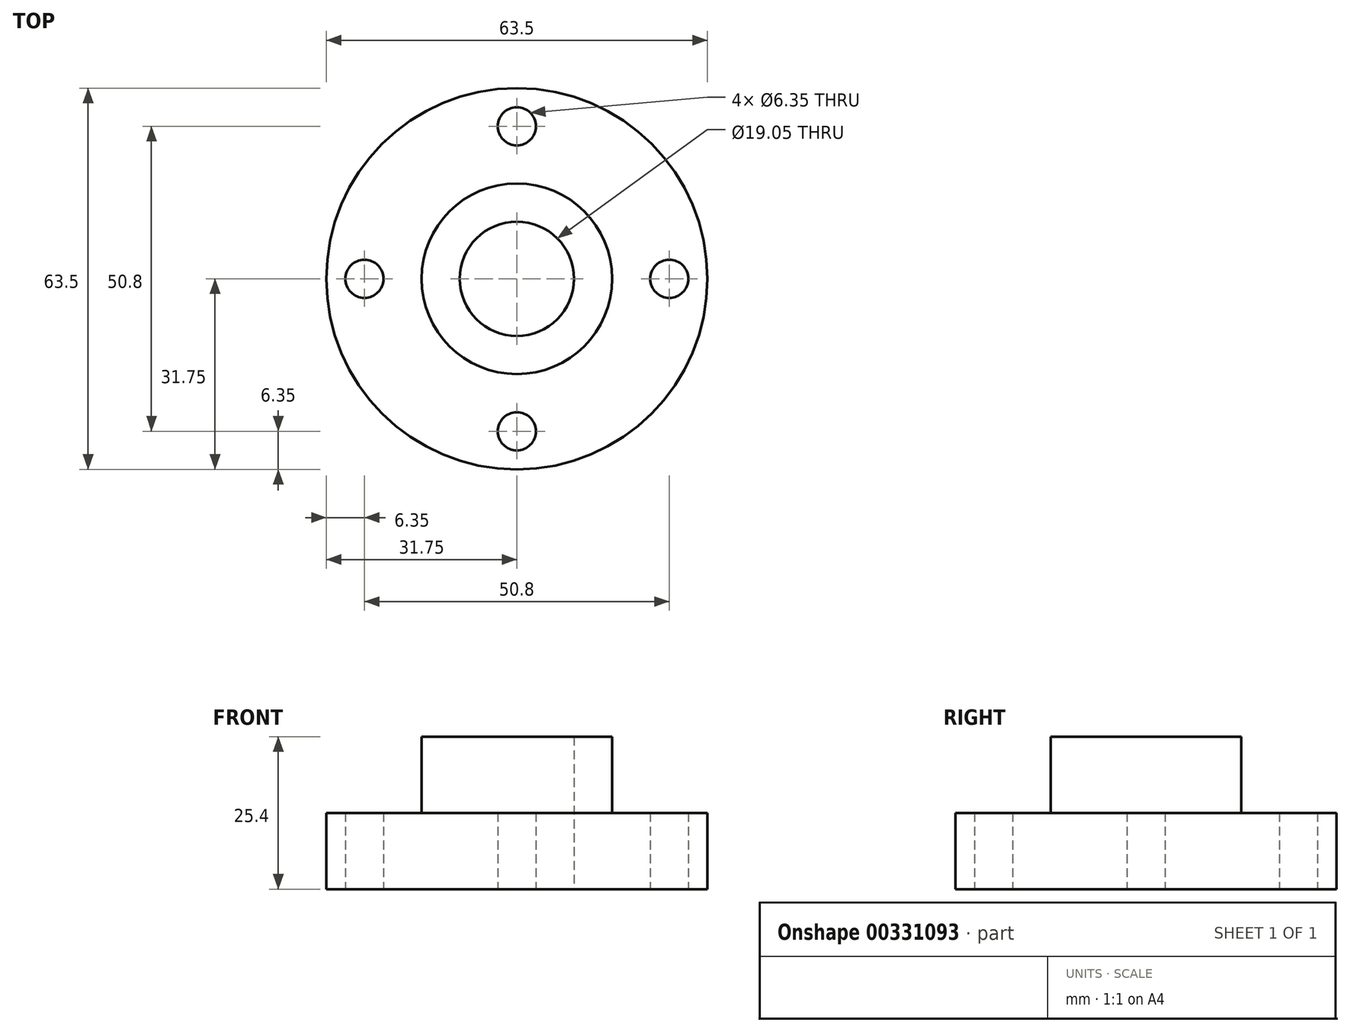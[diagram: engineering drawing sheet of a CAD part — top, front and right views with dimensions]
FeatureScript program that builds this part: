
annotation { "Feature Type Name" : "Feature", "Feature Type Description" : "" }
export const myFeature = defineFeature(function(context is Context, id is Id, definition is map)
    precondition{}
    {
        {
            var Q0;
            Q0=qCreatedBy(makeId("Top.planeOp"),FACE);
            var sketch = newSketch(context, id + "F0", { "sketchPlane" : qUnion([Q0])});
            skCircle(sketch, "E0", {"center": v(0, 0) * mm, "radius": 9.53 * mm});
            skCircle(sketch, "E1", {"center": v(0, 0) * mm, "radius": 15.88 * mm});
            skCircle(sketch, "E2", {"center": v(0, 0) * mm, "radius": 31.75 * mm});
            skCircle(sketch, "E3", {"center": v(0, 0) * mm, "radius": 25.4 * mm, "construction": true});
            skLineSegment(sketch, "E4", {"start": v(0, 37.73) * mm, "end": v(0, -36.34) * mm, "construction": true});
            skLineSegment(sketch, "E5", {"start": v(38.27, 0) * mm, "end": v(-35.65, 0) * mm, "construction": true});
            skPoint(sketch, "E6", {"position": v(-25.4, 0) * mm});
            skPoint(sketch, "E7", {"position": v(0, 25.4) * mm});
            skPoint(sketch, "E8", {"position": v(25.4, 0) * mm});
            skPoint(sketch, "E9", {"position": v(0, -25.4) * mm});
            skCircle(sketch, "E10", {"center": v(-25.4, 0) * mm, "radius": 3.18 * mm});
            skCircle(sketch, "E11", {"center": v(0, -25.4) * mm, "radius": 3.18 * mm});
            skCircle(sketch, "E12", {"center": v(25.4, 0) * mm, "radius": 3.18 * mm});
            skCircle(sketch, "E13", {"center": v(0, 25.4) * mm, "radius": 3.18 * mm});
            skSolve(sketch);
        }
        {
            var Q0;
            Q0=makeQuery(id+"F0.imprint","IMPRINT",FACE,{"disambiguationData":[TD([[makeQuery(id+"F0.imprint","IMPRINT",EDGE,{"derivedFrom":sQuery(id+"F0.wireOp",EDGE,"E0")}),-1.0]])]});
            extrude(context, id + "F1", {"entities" : qUnion([Q0]), "depth" : 25.4 * mm});
        }
        {
            var Q0;
            Q0=makeQuery(id+"F0.imprint","IMPRINT",FACE,{"disambiguationData":[TD([[makeQuery(id+"F0.imprint","IMPRINT",EDGE,{"derivedFrom":sQuery(id+"F0.wireOp",EDGE,"E1")}),-1.0]])]});
            extrude(context, id + "F2", {"entities" : qUnion([Q0]), "operationType" : NewBodyOperationType.ADD, "depth" : 12.7 * mm});
        }
    });
